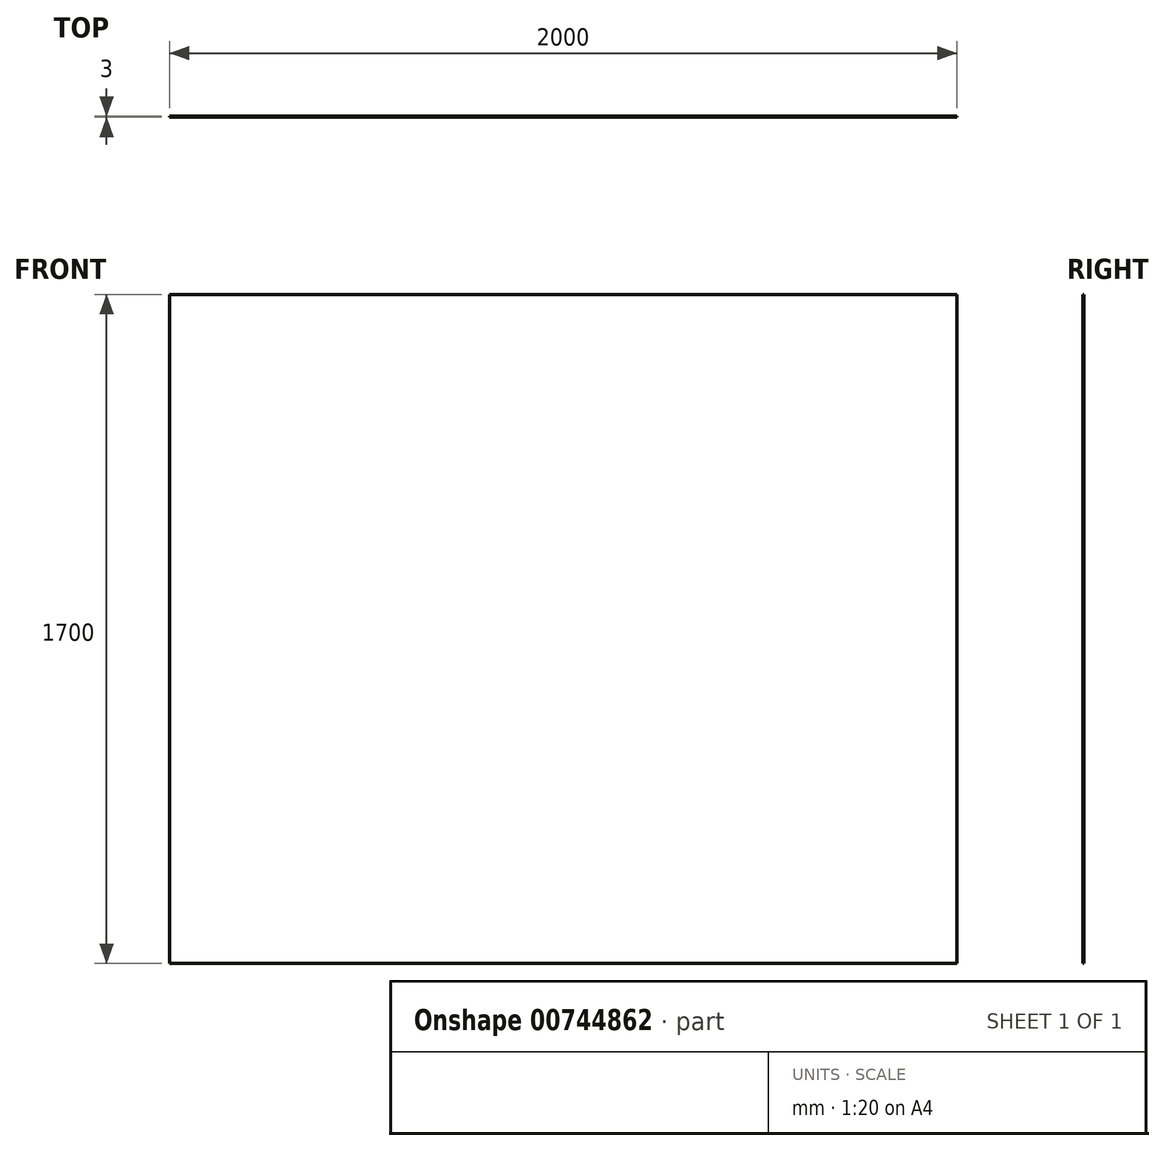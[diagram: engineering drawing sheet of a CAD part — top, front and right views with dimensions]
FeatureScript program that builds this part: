
annotation { "Feature Type Name" : "Feature", "Feature Type Description" : "" }
export const myFeature = defineFeature(function(context is Context, id is Id, definition is map)
    precondition{}
    {
        {
            var Q0;
            Q0=qCreatedBy(makeId("Front.planeOp"),FACE);
            var sketch = newSketch(context, id + "F0", { "sketchPlane" : qUnion([Q0])});
            skLineSegment(sketch, "E0.bottom", {"start": v(0, 0) * mm, "end": v(2000, 0) * mm});
            skLineSegment(sketch, "E0.top", {"start": v(0, 1700) * mm, "end": v(2000, 1700) * mm});
            skLineSegment(sketch, "E0.left", {"start": v(0, 0) * mm, "end": v(0, 1700) * mm});
            skLineSegment(sketch, "E0.right", {"start": v(2000, 0) * mm, "end": v(2000, 1700) * mm});
            skLineSegment(sketch, "E1.bottom", {"start": v(0, 1700) * mm, "end": v(100, 1700) * mm});
            skLineSegment(sketch, "E1.top", {"start": v(0, 1700) * mm, "end": v(100, 1700) * mm});
            skLineSegment(sketch, "E1.left", {"start": v(0, 1700) * mm, "end": v(0, 1700) * mm});
            skLineSegment(sketch, "E1.right", {"start": v(100, 1700) * mm, "end": v(100, 1700) * mm});
            skSolve(sketch);
        }
        {
            var Q0;
            Q0=makeQuery(id+"F0.imprint","IMPRINT",FACE,{"disambiguationData":[TD([[makeQuery(id+"F0.imprint","IMPRINT",EDGE,{"derivedFrom":sQuery(id+"F0.wireOp",EDGE,"E0.bottom")}),1.0]])]});
            extrude(context, id + "F1", {"entities" : qUnion([Q0]), "depth" : 3 * mm, "offsetDistance" : 25 * mm});
        }
    });
